# Revit family: Combi kettle Viking Combi 4G 400S_4224234
name_source: partatom
category: Specialty Equipment
revit_build: Autodesk Revit 2018 (Build: 20170223_1515(x64)
units: mm (PartAtom-declared; Revit-internal decimal feet)

## family parameters
Always vertical = Yes
Cut with Voids When Loaded = No
OmniClass Number = 23.40.40.14.17.11
OmniClass Title = Cookers, Ovens, Stoves
Part Type = Normal
Room Calculation Point = No
Round Connector Dimension = Use Diameter
Shared = No
Work Plane-Based = No

## types (1)
- Combi kettle Viking Combi 4G 400S_4224234
    Capacity = 400 L
    Cold Water Connection Height = 270 mm  [stored 0.885827 ft]
    Cold Water Flow = 20.0 L/min
    Cold Water Maximum Pressure = 600000.0 Pa
    Cold Water Minimum Pressure = 250000.0 Pa
    Cold Water Size = "R½"" (Ø15)"
    Condensate Return Connection Height = 0 mm  [stored 0 ft]
    Condensate Return Size = "R3/4"""
    Conn Plug = 2
    Cycle = 50 Hz
    Depth Actual = 1100 mm
    Description = Combi kettle Viking Combi 4G 400S
    Description_FI = Kombipata Viking Combi 4G 400S
    Description_NO = Kombigryte Viking Combi 4G 400S
    Description_SE = Kombigryta Viking Combi 4G 400S
    Direct Waste Connection Height = 0 mm  [stored 0 ft]
    Direct Waste Flow = 0.0 L/min
    Elec Conn Connection Height = 510 mm  [stored 1.67323 ft]
    Electrical protection rating = X5
    FL Amps = 25 A
    Foodservice Equipment Identifier = Yes
    Height Actual = 1050 mm
    Hot Water Connection Height = 270 mm  [stored 0.885827 ft]
    Hot Water Flow = 0.0 L/min
    Hot Water Maximum Pressure = 600000.0 Pa
    Hot Water Minimum Pressure = 250000.0 Pa
    Hot Water Size = "R½"" (Ø15)"
    Item Number = 4224234
    Latent Heat Output = 0 W
    Length Actual = 1560 mm  [stored 5.11811 ft]
    Metos Phase  = 3NPE
    Operational Current = 20 A
    Price = 0 $
    Refrigerant Mass = 0.00 kg
    Sensitive Heat Output = 0 W
    Steam Pounds per Hour = 115
    Steam Supply Connection Height = 140 mm  [stored 0.459318 ft]
    Steam Supply Maximum Pressure = 0.0 Pa
    Steam Supply Maximum Temperature = 130 °C
    Steam Supply Minimum Pressure = 100000.0 Pa
    Steam Supply Size = "R1 1/4"""
    URL Manufacturer = https://www.metos.com
    Volts = 400 V
    Watts = 4800 W
    Weight = 470

note: [stored X ft] marks values corroborated as IEEE doubles in the binary element streams (Revit-internal decimal feet)

## geometry (parser evidence)
native form markers: Sweep x2
no freeform markers — native parametric forms only
